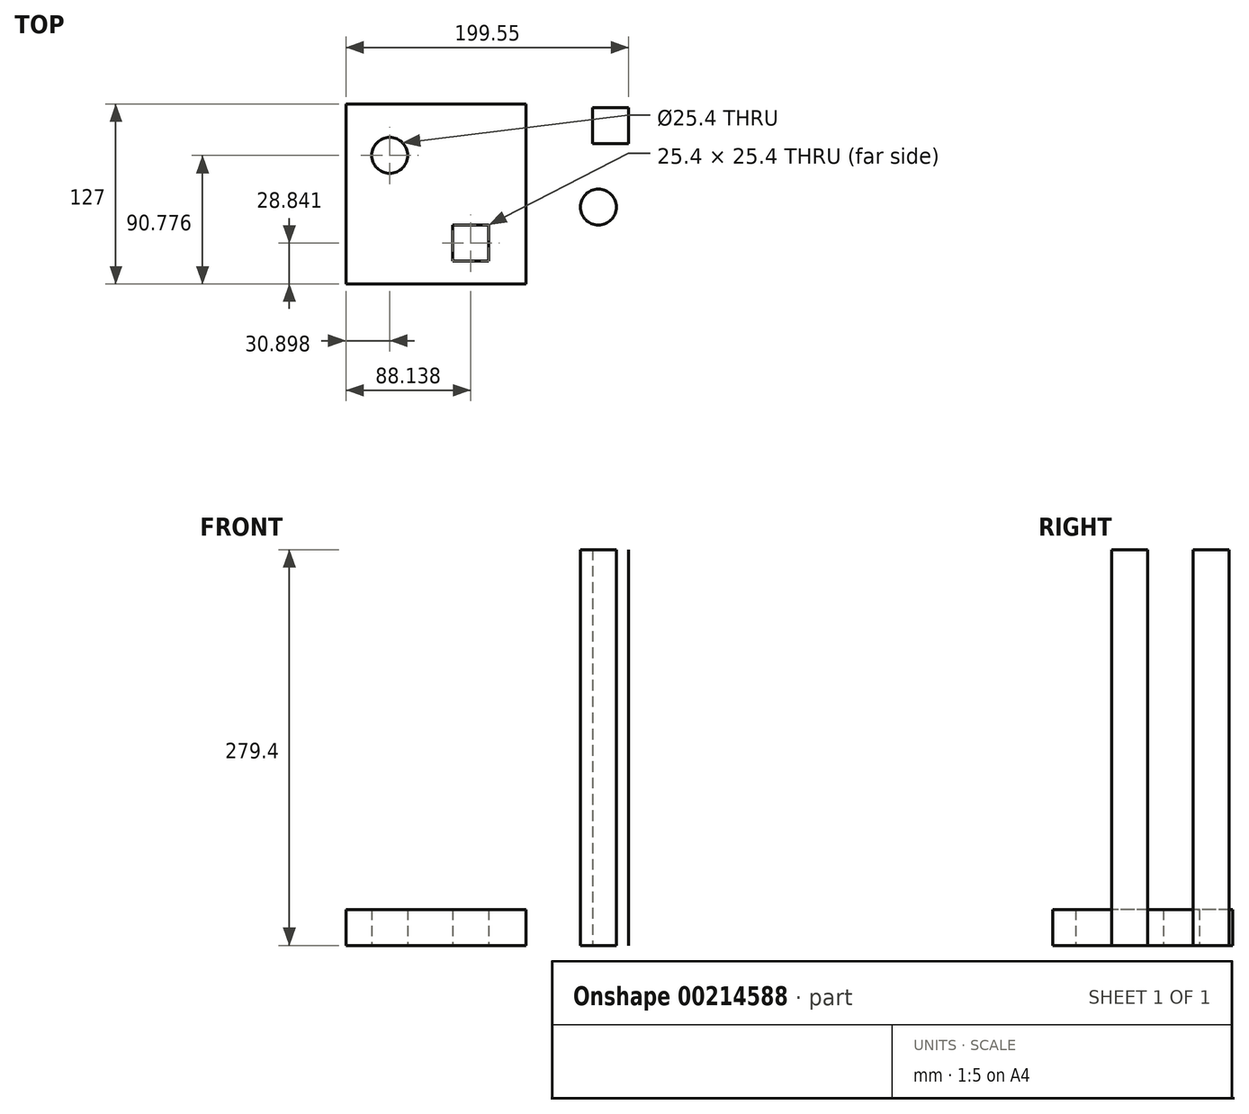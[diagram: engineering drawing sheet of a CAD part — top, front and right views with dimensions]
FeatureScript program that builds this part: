
annotation { "Feature Type Name" : "Feature", "Feature Type Description" : "" }
export const myFeature = defineFeature(function(context is Context, id is Id, definition is map)
    precondition{}
    {
        {
            var Q0;
            Q0=qCreatedBy(makeId("Top.planeOp"),FACE);
            var sketch = newSketch(context, id + "F0", { "sketchPlane" : qUnion([Q0])});
            skLineSegment(sketch, "E0.bottom", {"start": v(63.5, 63.5) * mm, "end": v(-63.5, 63.5) * mm});
            skLineSegment(sketch, "E0.top", {"start": v(63.5, -63.5) * mm, "end": v(-63.5, -63.5) * mm});
            skLineSegment(sketch, "E0.left", {"start": v(63.5, 63.5) * mm, "end": v(63.5, -63.5) * mm});
            skLineSegment(sketch, "E0.right", {"start": v(-63.5, 63.5) * mm, "end": v(-63.5, -63.5) * mm});
            skPoint(sketch, "E0.middle", {"position": v(0, 0) * mm});
            skCircle(sketch, "E1", {"center": v(-32.6, 27.28) * mm, "radius": 12.7 * mm});
            skLineSegment(sketch, "E2.bottom", {"start": v(11.94, -21.96) * mm, "end": v(37.34, -21.96) * mm});
            skLineSegment(sketch, "E2.top", {"start": v(11.94, -47.36) * mm, "end": v(37.34, -47.36) * mm});
            skLineSegment(sketch, "E2.left", {"start": v(11.94, -21.96) * mm, "end": v(11.94, -47.36) * mm});
            skLineSegment(sketch, "E2.right", {"start": v(37.34, -21.96) * mm, "end": v(37.34, -47.36) * mm});
            skLineSegment(sketch, "E3.bottom", {"start": v(110.65, 61.1) * mm, "end": v(136.05, 61.1) * mm});
            skLineSegment(sketch, "E3.top", {"start": v(110.65, 35.7) * mm, "end": v(136.05, 35.7) * mm});
            skLineSegment(sketch, "E3.left", {"start": v(110.65, 61.1) * mm, "end": v(110.65, 35.7) * mm});
            skLineSegment(sketch, "E3.right", {"start": v(136.05, 61.1) * mm, "end": v(136.05, 35.7) * mm});
            skCircle(sketch, "E4", {"center": v(114.66, -9.24) * mm, "radius": 12.7 * mm});
            skSolve(sketch);
        }
        {
            var Q0;
            Q0 = qSketchRegion(id + "F0", true);
            extrude(context, id + "F1", {"entities" : qUnion([Q0]), "depth" : 25.4 * mm});
        }
        {
            var Q0;
            Q0=makeQuery(id+"F1.opExtrude","CAP_FACE",FACE,{"disambiguationData":[OSD([sQuery(id+"F0.wireOp",EDGE,"E4")])],"isStart":false});
            var Q1;
            Q1=makeQuery(id+"F1.opExtrude","CAP_FACE",FACE,{"disambiguationData":[OSD([sQuery(id+"F0.wireOp",EDGE,"E3.bottom"),sQuery(id+"F0.wireOp",EDGE,"E3.top"),sQuery(id+"F0.wireOp",EDGE,"E3.left"),sQuery(id+"F0.wireOp",EDGE,"E3.right")])],"isStart":false});
            extrude(context, id + "F2", {"entities" : qUnion([Q0, Q1]), "operationType" : NewBodyOperationType.ADD, "depth" : 254 * mm});
        }
    });
